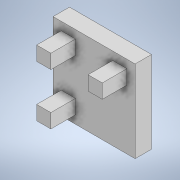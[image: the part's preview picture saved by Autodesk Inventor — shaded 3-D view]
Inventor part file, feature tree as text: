
AUTODESK INVENTOR PART (.ipt)
format: ipt  version: 2021 (Build 250183000, 183)  size: 130,048 bytes
history: native  units: in
note: dims shown in document units (in); Inventor stores cm internally (conversion verified against a paired STEP export)
features: extrude x2, sketch x2
ambient origin geometry x8: Origin, YZ Plane, XZ Plane, XY Plane, X Axis, Y Axis, Z Axis, Center Point
bodies: Solid1 (feature_tree)
feature tree (4):
  extrude  "Extrusion1"  Depth=1.9685in
  extrude  "Extrusion2"  Depth=0.1969in
  sketch  "Sketch1"  dims[d0=1.9685in d1=1.9685in]
  sketch  "Sketch3"  dims[d2=0.3937in d3=0.0in d8=0.1969in d9=0.1969in d10=0.3406in d11=0.3406in d12=0.1969in d13=0.3406in d14=0.3406in d15=0.1969in d16=0.1969in d17=0.1969in d18=0.3406in d19=0.3406in d20=0.5906in d21=0.0in]
